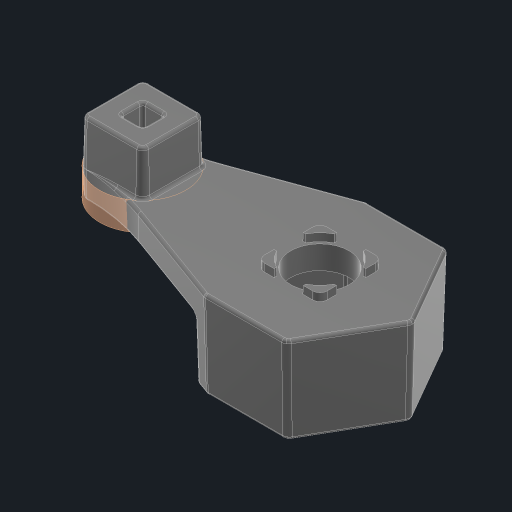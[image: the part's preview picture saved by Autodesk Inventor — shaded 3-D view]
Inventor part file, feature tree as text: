
AUTODESK INVENTOR PART (.ipt)
format: ipt  version: 2023 (Build 270158030, 158C)  size: 607,232 bytes
history: native  units: in
note: dims shown in document units (in); Inventor stores cm internally (conversion verified against a paired STEP export)
features: extrude x2, sketch x2, other x1, fillet x1
ambient origin geometry x8: Origin, YZ Plane, XZ Plane, XY Plane, X Axis, Y Axis, Z Axis, Center Point
bodies: Solid1 (feature_tree)
feature tree (6):
  extrude  "Extrusion1"  Depth=0.3937in TaperAngle=0.0deg
  sketch  "Sketch1"  dims[d0=0.0606in d1=0.0in d2=0.3937in d3=0.0in]
  other  "Srf1"
  sketch  "Sketch2"
  fillet  "Fillet10"  [1 undecoded]
  extrude  "ExtrusionSrf1"  [1 undecoded]
note: 2 required parameter values undecoded (feature->parameter linkage not recoverable at this tier; creation-order binding heuristic only, values carry confidence <= 0.55)
